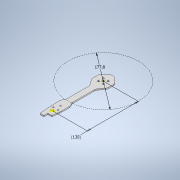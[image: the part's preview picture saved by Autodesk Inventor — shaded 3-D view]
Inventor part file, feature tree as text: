
AUTODESK INVENTOR PART (.ipt)
format: ipt  version: 2020 (Build 240168000, 168)  size: 245,760 bytes
history: native  units: in
note: dims shown in document units (in); Inventor stores cm internally (conversion verified against a paired STEP export)
features: sketch x3, extrude x2, fillet x1
ambient origin geometry x8: Origin, YZ Plane, XZ Plane, XY Plane, X Axis, Y Axis, Z Axis, Center Point
bodies: Body1 (feature_tree)
feature tree (6):
  extrude  "Extrusion1"  Depth=0.1181in
  sketch  "Sketch4"  dims[d7=0.4724in d8=5.1181in d9=7.0in]
  extrude  "Extrusion2"  Depth=5.1181in
  fillet  "Fillet1"  Radius=7.0in
  sketch  "Sketch3"  dims[d2=0.1181in d3=0.0in d4=0.8352in]
  sketch  "Sketch5"  dims[d10=5.1181in d11=0.2953in d12=0.2953in d13=0.9835in d14=0.9835in d15=0.989in d16=0.1181in d17=0.0in d18=0.3937in d19=0.3937in]
